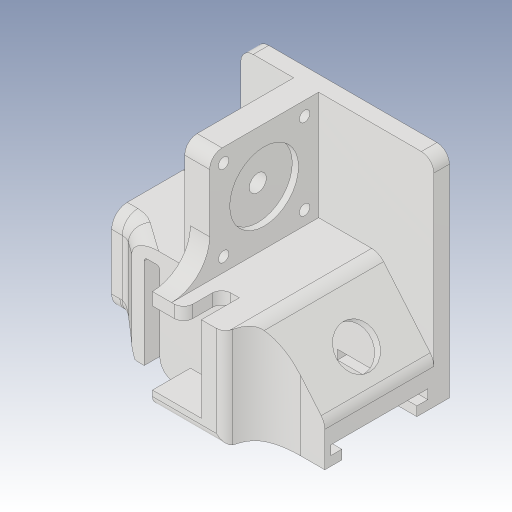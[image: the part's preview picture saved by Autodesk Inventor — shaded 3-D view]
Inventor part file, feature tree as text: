
AUTODESK INVENTOR PART (.ipt)
format: ipt  version: 2023.3 (Build 273359000, 359)  size: 941,056 bytes
history: native  units: in
note: dims shown in document units (in); Inventor stores cm internally (conversion verified against a paired STEP export)
features: sketch x20, extrude x12, fillet x10, hole x8, loft x3, plane x2, chamfer x2, sweep x1, projected_geometry x1
ambient origin geometry x8: Origin, YZ Plane, XZ Plane, XY Plane, X Axis, Y Axis, Z Axis, Center Point
bodies: Body1 (feature_tree)
feature tree (59):
  sketch  "Skizze3"  dims[d4=2.7165in d7=0.8701in]
  extrude  "Extrusion3"  Depth=0.8701in
  extrude  "Extrusion4"  Depth=0.3937in
  sketch  "Skizze47"  dims[d457=0.2559in d459=0.2362in]
  hole  "Bohrung19"  [1 undecoded]
  extrude  "Extrusion5"  Depth=1.378in TaperAngle=0.0deg
  sketch  "Skizze29"  dims[d10=0.8933in d12=0.1969in]
  hole  "Bohrung9"  [1 undecoded]
  hole  "Bohrung10"  [1 undecoded]
  extrude  "Extrusion27"  Depth=0.2559in
  hole  "Bohrung24"  [1 undecoded]
  fillet  "Rundung16"  Radius=0.315in
  sketch  "Skizze30"  dims[d16=2.4409in d18=1.378in d19=0.0in]
  plane  "Arbeitsebene11"
  sketch  "Skizze33"  dims[d38=0.0984in d88=0.2835in]
  extrude  "Extrusion28"  Depth=1.0236in
  sweep  "Sweeping3"
  fillet  "Rundung17"  Radius=0.3937in
  fillet  "Rundung18"  Radius=0.1969in
  fillet  "Rundung19"  Radius=0.1575in
  hole  "Bohrung12"  [1 undecoded]
  extrude  "Extrusion29"  Depth=0.1374in
  hole  "Bohrung14"  [1 undecoded]
  extrude  "Extrusion30"  Depth=0.1181in
  fillet  "Rundung21"  Radius=0.4724in
  sketch  "Skizze40"  dims[d426=0.2165in d427=0.2362in d428=0.1575in d429=0.0787in d430=90.0deg d431=0.1969in d432=0.0in]
  plane  "Arbeitsebene12"
  sketch  "Skizze41"  dims[d433=0.1339in d434=0.2362in d435=0.2559in d436=0.1339in d437=0.5635in d438=0.315in d439=0.0in d441=0.4724in d442=0.3937in d450=0.1969in d451=0.0in d452=0.1575in]
  extrude  "Extrusion31"  Depth=0.2362in
  loft  "Erhebung18"
  loft  "Erhebung20"
  loft  "Erhebung21"
  chamfer  "Fase3"  Distance=0.8701in
  extrude  "Extrusion33"  Depth=0.3937in TaperAngle=0.0deg
  fillet  "Rundung22"  Radius=1.0856in
  hole  "Bohrung17"  [1 undecoded]
  fillet  "Rundung23"  Radius=0.5906in
  fillet  "Rundung25"  [1 undecoded]
  extrude  "Extrusion36"  Depth=0.3937in
  fillet  "Rundung26"  Radius=0.315in
  fillet  "Rundung27"  Radius=0.1969in
  hole  "Bohrung20"  [1 undecoded]
  extrude  "Extrusion37"  Depth=0.3937in TaperAngle=0.0deg
  extrude  "Extrusion38"  Depth=0.3937in
  sketch  "Skizze53"  dims[d476=0.1181in d477=0.2362in d478=0.1575in d479=0.0787in d480=90.0deg d481=0.2756in d482=0.0in d483=0.8701in d484=0.0787in d485=0.0in d500=1.0856in d501=0.2362in d502=0.5118in d503=0.6299in d504=0.1575in d505=0.0787in d506=90.0deg d507=0.315in d508=0.8108in d509=0.5906in d510=90.0deg d512=0.1575in d513=0.315in d514=0.1969in d516=1.378in d517=0.315in d518=0.0in d519=0.0394in d533=0.0197in d534=0.9449in d535=0.9449in d537=0.1969in d538=0.9449in d539=0.6299in d540=0.7874in d541=0.7874in d542=1.1024in d543=1.1024in d546=0.1969in d547=0.0in d556=0.0in d557=90.0deg d558=0.0in d559=90.0deg d566=0.1575in d567=0.1181in d568=0.0787in d569=0.3937in d570=0.1181in d571=0.3937in d572=0.1575in d573=0.0in d574=90.0deg d575=0.0in d576=90.0deg d577=0.0in d578=90.0deg d581=0.1575in d582=0.0787in d583=0.0in d584=90.0deg d585=0.0787in d586=0.2165in d587=45.0deg d588=0.1969in d589=0.0in d590=0.1969in d604=0.0617in d605=0.1575in d606=0.1575in d607=0.0787in d608=90.0deg d609=0.248in d610=0.0in d624=0.1969in d626=0.0394in d629=0.1339in d630=0.2362in d631=0.2559in d632=0.1339in d633=90.0deg d634=0.3465in d635=0.0in d636=0.5846in d638=0.1575in d639=0.4803in d640=0.0in d641=0.9213in d642=0.189in d643=0.6181in d644=0.4803in d645=0.1181in d646=1.0945in d647=0.0846in d648=0.0669in d649=0.2362in d650=0.2559in d651=0.1339in d652=90.0deg d653=0.3465in d654=0.0in d655=0.3937in d657=0.1378in d658=0.5512in d683=0.2756in d684=0.1339in d685=0.2362in d686=0.2559in d687=0.1339in d688=90.0deg d689=0.7874in d690=0.0in d691=0.1969in d692=0.1457in d693=0.2165in d694=0.3937in d695=0.2756in d696=0.5413in d697=0.1378in d698=0.1181in d699=0.1181in d700=1.0039in d701=0.0in d702=0.0433in d703=1.0039in d704=0.0in d705=0.3937in d706=0.3937in d707=0.5906in d708=0.5906in d709=0.0591in d710=0.0787in d711=45.0deg d98=0.0197in d99=0.0344in d100=0.0197in d104=0.0197in d105=0.0344in d106=0.0197in d107=0.0344in d108=0.0344in d265=0.0197in d266=0.0344in d267=0.0197in d268=0.0344in d418=0.0197in d419=0.0344in d420=0.0197in d421=0.0344in d496=0.0197in d497=0.0344in d498=0.0197in d499=0.0344in]
  chamfer  "Fase4"  Distance=0.0197in
  sketch  "Skizze4"  dims[d8=0.8661in d9=0.3937in]
  sketch  "Skizze32"  dims[d20=0.9488in d21=0.0in d29=0.0in d30=0.0in]
  sketch  "Skizze34"  dims[d101=0.2559in d102=0.2559in]
  sketch  "Skizze36"  dims[d308=0.4114in d309=0.0in d364=0.0197in d423=0.315in]
  sketch  "Skizze37"  dims[d424=1.0236in d425=1.0236in]
  sketch  "Skizze43"  dims[d453=0.3937in d454=0.4724in]
  sketch  "Skizze44"  dims[d455=0.4331in d456=0.1374in]
  projected_geometry  "Projizierte Kontur18"
  sketch  "Skizze48"  dims[d461=0.3543in d462=0.1181in d465=0.4724in]
  sketch  "Skizze49"  dims[d466=0.2362in d467=0.2362in]
  sketch  "Skizze50"  dims[d468=0.1575in d469=0.0in d470=0.0689in]
  sketch  "Skizze51"  dims[d471=0.0in d472=0.0in d473=0.2362in]
  sketch  "Skizze52"  dims[d474=0.0787in d475=0.0354in]
note: 9 required parameter values undecoded (feature->parameter linkage not recoverable at this tier; creation-order binding heuristic only, values carry confidence <= 0.55)
